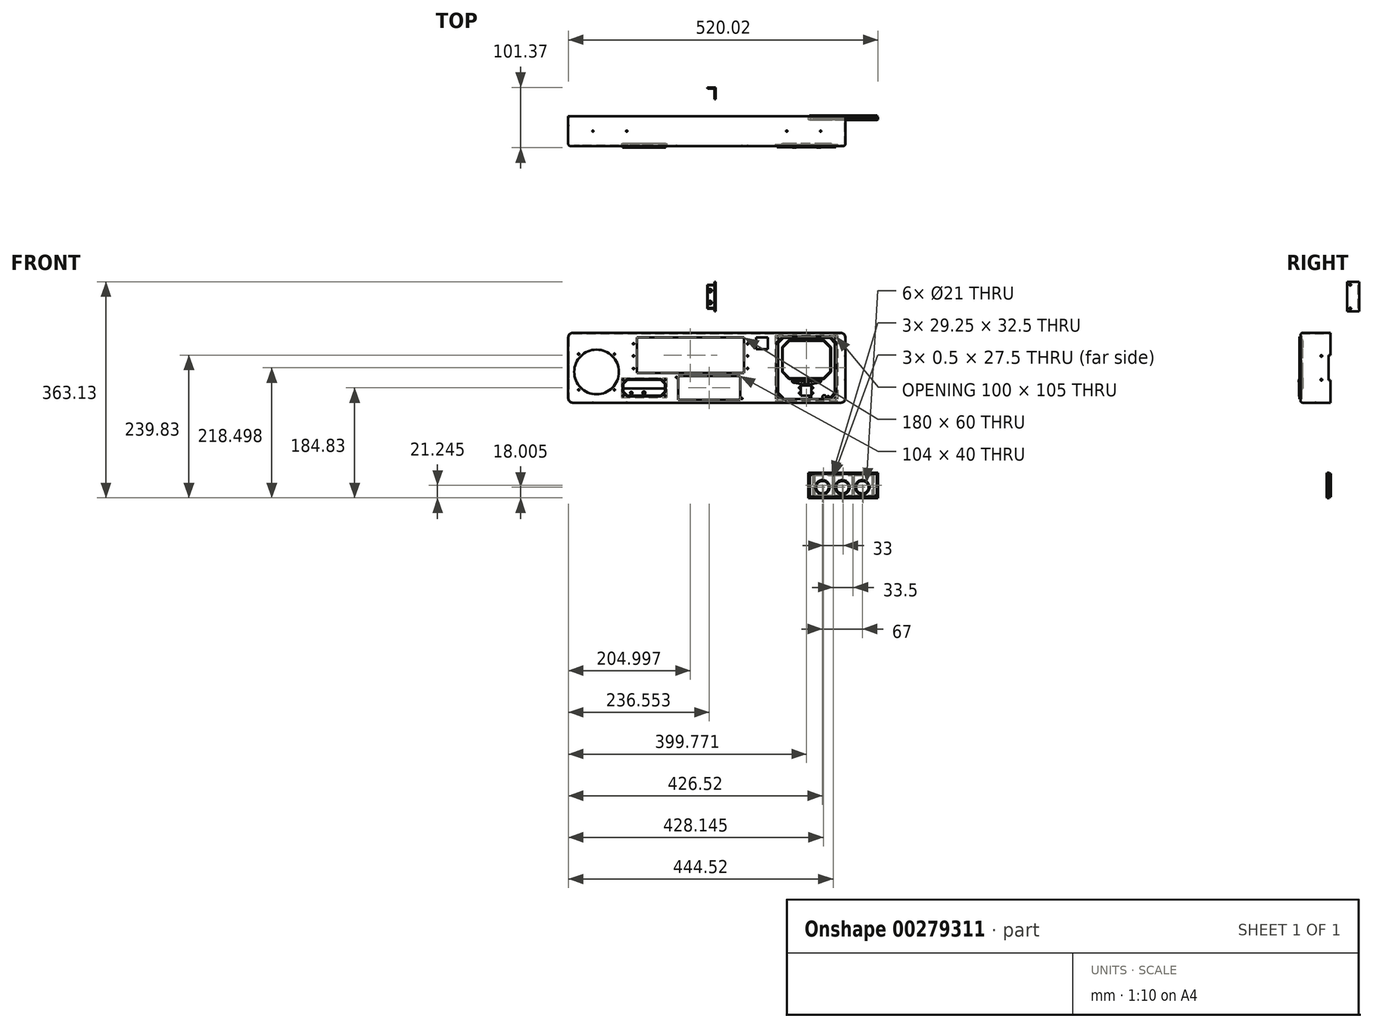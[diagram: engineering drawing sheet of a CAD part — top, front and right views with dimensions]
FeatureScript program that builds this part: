
annotation { "Feature Type Name" : "Feature", "Feature Type Description" : "" }
export const myFeature = defineFeature(function(context is Context, id is Id, definition is map)
    precondition{}
    {
        {
            var Q0;
            Q0=qCreatedBy(makeId("Front.planeOp"),FACE);
            var sketch = newSketch(context, id + "F0", { "sketchPlane" : qUnion([Q0])});
            skLineSegment(sketch, "E0.bottom", {"start": v(-245.15, 85.69) * mm, "end": v(219.85, 85.69) * mm});
            skLineSegment(sketch, "E0.top", {"start": v(-245.15, -31.31) * mm, "end": v(219.85, -31.31) * mm});
            skLineSegment(sketch, "E0.left", {"start": v(-245.15, 85.69) * mm, "end": v(-245.15, -31.31) * mm});
            skLineSegment(sketch, "E0.right", {"start": v(219.85, 85.69) * mm, "end": v(219.85, -31.31) * mm});
            skSolve(sketch);
        }
        {
            var Q0;
            Q0=qSketchRegion(id+"F0",true);
            var Q1;
            Q1=makeQuery(id+"F0.imprint","IMPRINT",FACE,{"disambiguationData":[TD([[makeQuery(id+"F0.imprint","IMPRINT",EDGE,{"derivedFrom":sQuery(id+"F0.wireOp",EDGE,"E0.bottom")}),-1.0]])]});
            extrude(context, id + "F1", {"entities" : qUnion([Q0, Q1]), "depth" : 50 * mm});
        }
        {
            var Q0;
            Q0=makeQuery(id+"F1.opExtrude","CAP_FACE",FACE,{"disambiguationData":[OSD([sQuery(id+"F0.wireOp",EDGE,"E0.bottom"),sQuery(id+"F0.wireOp",EDGE,"E0.top"),sQuery(id+"F0.wireOp",EDGE,"E0.left"),sQuery(id+"F0.wireOp",EDGE,"E0.right")])],"isStart":true});
            shell(context, id + "F2", {"entities" : qUnion([Q0]), "thickness" : 1 * mm});
        }
        {
            var Q0;
            Q0=makeQuery(id+"F1.opExtrude","CAP_FACE",FACE,{"disambiguationData":[OSD([sQuery(id+"F0.wireOp",EDGE,"E0.bottom"),sQuery(id+"F0.wireOp",EDGE,"E0.top"),sQuery(id+"F0.wireOp",EDGE,"E0.left"),sQuery(id+"F0.wireOp",EDGE,"E0.right")])],"isStart":false});
            var sketch = newSketch(context, id + "F3", { "sketchPlane" : qUnion([Q0])});
            skLineSegment(sketch, "E1.bottom", {"start": v(-130.15, 78.52) * mm, "end": v(49.85, 78.52) * mm});
            skLineSegment(sketch, "E1.top", {"start": v(-130.15, 18.52) * mm, "end": v(49.85, 18.52) * mm});
            skLineSegment(sketch, "E1.left", {"start": v(-130.15, 78.52) * mm, "end": v(-130.15, 18.52) * mm});
            skLineSegment(sketch, "E1.right", {"start": v(49.85, 78.52) * mm, "end": v(49.85, 18.52) * mm});
            skLineSegment(sketch, "E2.bottom", {"start": v(69.85, 78.32) * mm, "end": v(89.85, 78.32) * mm});
            skLineSegment(sketch, "E2.top", {"start": v(69.85, 58.32) * mm, "end": v(89.85, 58.32) * mm});
            skLineSegment(sketch, "E2.left", {"start": v(69.85, 78.32) * mm, "end": v(69.85, 58.32) * mm});
            skLineSegment(sketch, "E2.right", {"start": v(89.85, 78.32) * mm, "end": v(89.85, 58.32) * mm});
            skLineSegment(sketch, "E3.bottom", {"start": v(114.52, 79.69) * mm, "end": v(194.72, 79.69) * mm});
            skLineSegment(sketch, "E3.top", {"start": v(114.52, -25.31) * mm, "end": v(194.72, -25.31) * mm});
            skLineSegment(sketch, "E3.left", {"start": v(104.62, 69.79) * mm, "end": v(104.62, -15.41) * mm});
            skLineSegment(sketch, "E3.right", {"start": v(204.62, 69.79) * mm, "end": v(204.62, -15.41) * mm});
            skLineSegment(sketch, "E4.bottom", {"start": v(-128.05, -55.46) * mm, "end": v(-35.05, -55.46) * mm, "construction": true});
            skLineSegment(sketch, "E4.top", {"start": v(-128.05, -91.46) * mm, "end": v(-35.05, -91.46) * mm, "construction": true});
            skLineSegment(sketch, "E4.left", {"start": v(-128.05, -55.46) * mm, "end": v(-128.05, -91.46) * mm, "construction": true});
            skLineSegment(sketch, "E4.right", {"start": v(-35.05, -55.46) * mm, "end": v(-35.05, -91.46) * mm, "construction": true});
            skCircle(sketch, "E5", {"center": v(55.74, 67.55) * mm, "radius": 1.1 * mm});
            skCircle(sketch, "E6", {"center": v(55.74, 47.16) * mm, "radius": 1.1 * mm});
            skCircle(sketch, "E7", {"center": v(55.74, 26.05) * mm, "radius": 1.1 * mm});
            skLineSegment(sketch, "E8.bottom", {"start": v(-233.81, -59.67) * mm, "end": v(-156.81, -59.67) * mm, "construction": true});
            skLineSegment(sketch, "E8.top", {"start": v(-233.81, -136.67) * mm, "end": v(-156.81, -136.67) * mm, "construction": true});
            skLineSegment(sketch, "E8.left", {"start": v(-233.81, -59.67) * mm, "end": v(-233.81, -136.67) * mm, "construction": true});
            skLineSegment(sketch, "E8.right", {"start": v(-156.81, -59.67) * mm, "end": v(-156.81, -136.67) * mm, "construction": true});
            skCircle(sketch, "E9", {"center": v(106.12, 78.19) * mm, "radius": 1.1 * mm});
            skLineSegment(sketch, "E10", {"start": v(104.62, 69.79) * mm, "end": v(114.52, 79.69) * mm});
            skCircle(sketch, "E11", {"center": v(63.6, -74.48) * mm, "radius": 9.5 * mm});
            skLineSegment(sketch, "E12.bottom", {"start": v(46.65, -54.77) * mm, "end": v(139.65, -54.77) * mm});
            skLineSegment(sketch, "E12.top", {"start": v(46.65, -90.77) * mm, "end": v(139.65, -90.77) * mm});
            skLineSegment(sketch, "E12.left", {"start": v(46.65, -54.77) * mm, "end": v(46.65, -90.77) * mm});
            skLineSegment(sketch, "E12.right", {"start": v(139.65, -54.77) * mm, "end": v(139.65, -90.77) * mm});
            skCircle(sketch, "E13", {"center": v(93.62, -74.48) * mm, "radius": 9.5 * mm});
            skCircle(sketch, "E14", {"center": v(123.01, -74.48) * mm, "radius": 9.5 * mm});
            skCircle(sketch, "E15", {"center": v(50.65, -58.77) * mm, "radius": 1.5 * mm});
            skCircle(sketch, "E16", {"center": v(135.65, -86.77) * mm, "radius": 1.5 * mm});
            skLineSegment(sketch, "E17.bottom", {"start": v(-146.37, 8.19) * mm, "end": v(-89.37, 8.19) * mm});
            skLineSegment(sketch, "E17.top", {"start": v(-146.37, -20.81) * mm, "end": v(-89.37, -20.81) * mm});
            skLineSegment(sketch, "E17.left", {"start": v(-154.15, 0.4) * mm, "end": v(-154.15, -13.03) * mm});
            skLineSegment(sketch, "E17.right", {"start": v(-81.6, 0.4) * mm, "end": v(-81.6, -13.03) * mm});
            skLineSegment(sketch, "E18", {"start": v(104.62, -15.41) * mm, "end": v(114.52, -25.31) * mm});
            skLineSegment(sketch, "E19", {"start": v(194.72, -25.31) * mm, "end": v(204.62, -15.41) * mm});
            skLineSegment(sketch, "E20", {"start": v(194.72, 79.69) * mm, "end": v(204.62, 69.79) * mm});
            skCircle(sketch, "E21", {"center": v(105.72, -23.81) * mm, "radius": 1.1 * mm});
            skCircle(sketch, "E22", {"center": v(203.52, -23.81) * mm, "radius": 1.1 * mm});
            skCircle(sketch, "E23", {"center": v(203.12, 78.19) * mm, "radius": 1.1 * mm});
            skCircle(sketch, "E24", {"center": v(-197.65, 20.23) * mm, "radius": 37.5 * mm});
            skLineSegment(sketch, "E25", {"start": v(-154.15, 0.4) * mm, "end": v(-146.37, 8.19) * mm});
            skLineSegment(sketch, "E26", {"start": v(-89.37, 8.19) * mm, "end": v(-81.6, 0.4) * mm});
            skLineSegment(sketch, "E27", {"start": v(-81.6, -13.03) * mm, "end": v(-89.37, -20.81) * mm});
            skLineSegment(sketch, "E28", {"start": v(-154.15, -13.03) * mm, "end": v(-146.37, -20.81) * mm});
            skCircle(sketch, "E29", {"center": v(-135.7, 67.55) * mm, "radius": 1.1 * mm});
            skCircle(sketch, "E30", {"center": v(-135.7, 47.16) * mm, "radius": 1.1 * mm});
            skCircle(sketch, "E31", {"center": v(-135.7, 26.05) * mm, "radius": 1.1 * mm});
            skCircle(sketch, "E32", {"center": v(-227.65, 50.23) * mm, "radius": 1.1 * mm});
            skCircle(sketch, "E33", {"center": v(-227.65, -9.77) * mm, "radius": 1.1 * mm});
            skCircle(sketch, "E34", {"center": v(-167.65, -9.77) * mm, "radius": 1.1 * mm});
            skCircle(sketch, "E35", {"center": v(-167.65, 50.23) * mm, "radius": 1.1 * mm});
            skCircle(sketch, "E36", {"center": v(-63.6, 11.29) * mm, "radius": 1.1 * mm});
            skCircle(sketch, "E37", {"center": v(46.4, -24.21) * mm, "radius": 1.1 * mm});
            skLineSegment(sketch, "E38.bottom", {"start": v(-60.6, 13.52) * mm, "end": v(43.4, 13.52) * mm});
            skLineSegment(sketch, "E38.top", {"start": v(-60.6, -26.48) * mm, "end": v(43.4, -26.48) * mm});
            skLineSegment(sketch, "E38.left", {"start": v(-60.6, 13.52) * mm, "end": v(-60.6, -26.48) * mm});
            skLineSegment(sketch, "E38.right", {"start": v(43.4, 13.52) * mm, "end": v(43.4, -26.48) * mm});
            skLineSegment(sketch, "E39", {"start": v(-230.37, -45.58) * mm, "end": v(-80.37, -45.58) * mm, "construction": true});
            skLineSegment(sketch, "E40", {"start": v(-255.4, -26.53) * mm, "end": v(-255.4, 68.47) * mm, "construction": true});
            skLineSegment(sketch, "E41", {"start": v(-239.28, 22.84) * mm, "end": v(-239.28, -34.99) * mm, "construction": true});
            skLineSegment(sketch, "E42.bottom", {"start": v(-167.65, -9.77) * mm, "end": v(-227.65, -9.77) * mm, "construction": true});
            skLineSegment(sketch, "E42.top", {"start": v(-167.65, 50.23) * mm, "end": v(-227.65, 50.23) * mm, "construction": true});
            skLineSegment(sketch, "E42.left", {"start": v(-167.65, -9.77) * mm, "end": v(-167.65, 50.23) * mm, "construction": true});
            skLineSegment(sketch, "E42.right", {"start": v(-227.65, -9.77) * mm, "end": v(-227.65, 50.23) * mm, "construction": true});
            skSolve(sketch);
        }
        {
            var Q0;
            Q0=makeQuery(id+"F1.opExtrude","SWEPT_EDGE",EDGE,{"disambiguationData":[OSD([sQuery(id+"F0.wireOp",EDGE,"E0.bottom"),sQuery(id+"F0.wireOp",EDGE,"E0.left")])]});
            var Q1;
            Q1=makeQuery(id+"F1.opExtrude","SWEPT_EDGE",EDGE,{"disambiguationData":[OSD([sQuery(id+"F0.wireOp",EDGE,"E0.bottom"),sQuery(id+"F0.wireOp",EDGE,"E0.right")])]});
            var Q2;
            Q2=makeQuery(id+"F1.opExtrude","SWEPT_EDGE",EDGE,{"disambiguationData":[OSD([sQuery(id+"F0.wireOp",EDGE,"E0.top"),sQuery(id+"F0.wireOp",EDGE,"E0.right")])]});
            var Q3;
            Q3=makeQuery(id+"F1.opExtrude","SWEPT_EDGE",EDGE,{"disambiguationData":[OSD([sQuery(id+"F0.wireOp",EDGE,"E0.top"),sQuery(id+"F0.wireOp",EDGE,"E0.left")])]});
            var Q4;
            Q4=makeQuery(id+"F2.opShell","OFFSET_EDGE",EDGE,{"disambiguationData":[OSD([sQuery(id+"F0.wireOp",EDGE,"E0.bottom"),sQuery(id+"F0.wireOp",EDGE,"E0.left")])]});
            var Q5;
            Q5=makeQuery(id+"F2.opShell","OFFSET_EDGE",EDGE,{"disambiguationData":[OSD([sQuery(id+"F0.wireOp",EDGE,"E0.top"),sQuery(id+"F0.wireOp",EDGE,"E0.left")])]});
            var Q6;
            Q6=makeQuery(id+"F2.opShell","OFFSET_EDGE",EDGE,{"disambiguationData":[OSD([sQuery(id+"F0.wireOp",EDGE,"E0.top"),sQuery(id+"F0.wireOp",EDGE,"E0.right")])]});
            var Q7;
            Q7=makeQuery(id+"F2.opShell","OFFSET_EDGE",EDGE,{"disambiguationData":[OSD([sQuery(id+"F0.wireOp",EDGE,"E0.bottom"),sQuery(id+"F0.wireOp",EDGE,"E0.right")])]});
            fillet(context, id + "F4", {"entities" : qUnion([Q0, Q1, Q2, Q3, Q4, Q5, Q6, Q7]), "radius" : 7 * mm, "tangentPropagation" : true, "allowEdgeOverflow" : false});
        }
        {
            var Q0;
            Q0=qSketchRegion(id+"F3",true);
            extrude(context, id + "F5", {"entities" : qUnion([Q0]), "operationType" : NewBodyOperationType.REMOVE, "oppositeDirection" : true, "depth" : 25 * mm});
        }
        {
            var Q0;
            {var subQ0=sQuery(id+"F0.wireOp",EDGE,"E0.right");var subQ1=sQuery(id+"F0.wireOp",EDGE,"E0.bottom");Q0=makeQuery(id+"F4.opFillet","BLEND_EDGE",EDGE,{"blendedFrom":[makeQuery(id+"F1.opExtrude","SWEPT_EDGE",EDGE,{"disambiguationData":[OSD([subQ1,subQ0])]}),makeQuery(id+"F1.opExtrude","CAP_FACE",FACE,{"disambiguationData":[OSD([subQ1,sQuery(id+"F0.wireOp",EDGE,"E0.top"),sQuery(id+"F0.wireOp",EDGE,"E0.left"),subQ0])],"isStart":false})],"blendedInto":[makeQuery(id+"F1.opExtrude","CAP_FACE",FACE,{"disambiguationData":[OSD([subQ1,sQuery(id+"F0.wireOp",EDGE,"E0.top"),sQuery(id+"F0.wireOp",EDGE,"E0.left"),subQ0])],"isStart":false})]});}
            fillet(context, id + "F6", {"entities" : qUnion([Q0]), "radius" : 3 * mm, "tangentPropagation" : true, "allowEdgeOverflow" : false});
        }
        {
            var Q0;
            Q0=makeQuery(id+"F1.opExtrude","SWEPT_FACE",FACE,{"disambiguationData":[OSD([sQuery(id+"F0.wireOp",EDGE,"E0.left")])]});
            var sketch = newSketch(context, id + "F7", { "sketchPlane" : qUnion([Q0])});
            skCircle(sketch, "E43", {"center": v(15, 47.19) * mm, "radius": 1.5 * mm});
            skCircle(sketch, "E44", {"center": v(15, 7.19) * mm, "radius": 1.5 * mm});
            skLineSegment(sketch, "E45", {"start": v(-16.01, 27.19) * mm, "end": v(37.35, 27.19) * mm, "construction": true});
            skPoint(sketch, "E46.middle.positionSnap0", {"position": v(0, 27.19) * mm});
            skPoint(sketch, "E46.centerSnap0", {"position": v(0, 27.19) * mm});
            skLineSegment(sketch, "E47.bottom", {"start": v(3, 6.19) * mm, "end": v(0, 6.19) * mm});
            skLineSegment(sketch, "E47.top", {"start": v(3, 48.19) * mm, "end": v(0, 48.19) * mm});
            skLineSegment(sketch, "E47.left", {"start": v(3, 6.19) * mm, "end": v(3, 48.19) * mm});
            skLineSegment(sketch, "E47.right", {"start": v(0, 6.19) * mm, "end": v(0, 48.19) * mm});
            skPoint(sketch, "E47.middle", {"position": v(1.5, 27.19) * mm});
            skSolve(sketch);
        }
        {
            var Q0;
            Q0=qSketchRegion(id+"F7",true);
            extrude(context, id + "F8", {"entities" : qUnion([Q0]), "operationType" : NewBodyOperationType.REMOVE, "oppositeDirection" : true, "depth" : 500 * mm});
        }
        {
            var Q0;
            Q0=qCreatedBy(makeId("Right.planeOp"),FACE);
            var sketch = newSketch(context, id + "F9", { "sketchPlane" : qUnion([Q0])});
            skLineSegment(sketch, "E48.bottom", {"start": v(28.37, 121.82) * mm, "end": v(48.37, 121.82) * mm});
            skLineSegment(sketch, "E48.top", {"start": v(28.37, 171.82) * mm, "end": v(48.37, 171.82) * mm});
            skLineSegment(sketch, "E48.left", {"start": v(28.37, 121.82) * mm, "end": v(28.37, 171.82) * mm});
            skLineSegment(sketch, "E48.right", {"start": v(48.37, 121.82) * mm, "end": v(48.37, 171.82) * mm});
            skPoint(sketch, "E48.middle", {"position": v(38.37, 146.82) * mm});
            skCircle(sketch, "E49", {"center": v(33.37, 166.82) * mm, "radius": 1.5 * mm});
            skCircle(sketch, "E50", {"center": v(33.37, 126.82) * mm, "radius": 1.5 * mm});
            skSolve(sketch);
        }
        {
            var Q0;
            Q0=qSketchRegion(id+"F9",true);
            extrude(context, id + "F10", {"entities" : qUnion([Q0]), "depth" : 2 * mm});
        }
        {
            var Q0;
            Q0=makeQuery(id+"F10.opExtrude","SWEPT_FACE",FACE,{"disambiguationData":[OSD([sQuery(id+"F9.wireOp",EDGE,"E48.right")])]});
            var sketch = newSketch(context, id + "F11", { "sketchPlane" : qUnion([Q0])});
            skLineSegment(sketch, "E51.bottom", {"start": v(0, 166.82) * mm, "end": v(12, 166.82) * mm});
            skLineSegment(sketch, "E51.top", {"start": v(0, 126.82) * mm, "end": v(12, 126.82) * mm});
            skLineSegment(sketch, "E51.left", {"start": v(0, 166.82) * mm, "end": v(0, 126.82) * mm});
            skLineSegment(sketch, "E51.right", {"start": v(12, 166.82) * mm, "end": v(12, 126.82) * mm});
            skSolve(sketch);
        }
        {
            var Q0;
            Q0=qSketchRegion(id+"F11",true);
            extrude(context, id + "F12", {"entities" : qUnion([Q0]), "operationType" : NewBodyOperationType.ADD, "oppositeDirection" : true, "depth" : 2 * mm});
        }
        {
            var Q0;
            Q0=makeQuery(id+"F12.opExtrude","CAP_FACE",FACE,{"disambiguationData":[OSD([sQuery(id+"F11.wireOp",EDGE,"E51.bottom"),sQuery(id+"F11.wireOp",EDGE,"E51.top"),sQuery(id+"F11.wireOp",EDGE,"E51.left"),sQuery(id+"F11.wireOp",EDGE,"E51.right")])],"isStart":false});
            var sketch = newSketch(context, id + "F13", { "sketchPlane" : qUnion([Q0])});
            skCircle(sketch, "E52", {"center": v(-7, 156.82) * mm, "radius": 1.5 * mm});
            skCircle(sketch, "E53", {"center": v(-7, 136.82) * mm, "radius": 1.5 * mm});
            skSolve(sketch);
        }
        {
            var Q0;
            Q0=sQuery(id+"F13.wireOp",VERTEX,"E52.center");
            var Q1;
            Q1=sQuery(id+"F13.wireOp",VERTEX,"E53.center");
            var Q2;
            Q2=makeQuery(id+"F10.opExtrude","SWEPT_BODY",BODY,{"disambiguationData":[OSD([sQuery(id+"F9.wireOp",EDGE,"E48.bottom"),sQuery(id+"F9.wireOp",EDGE,"E48.top"),sQuery(id+"F9.wireOp",EDGE,"E48.left"),sQuery(id+"F9.wireOp",EDGE,"E48.right"),sQuery(id+"F9.wireOp",EDGE,"E49"),sQuery(id+"F9.wireOp",EDGE,"E50")])]});
            hole(context, id + "F14", {"style" : HoleStyle.C_SINK, "endStyle" : HoleEndStyle.THROUGH, "holeDiameter" : 3 * mm, "cSinkDiameter" : 5.7 * mm, "cSinkAngle" : 90 * degree, "locations" : qUnion([Q0, Q1]), "scope" : qUnion([Q2]), "isTappedThrough" : true});
        }
        {
            var Q0;
            Q0=makeQuery(id+"F12.opExtrude","CAP_EDGE",EDGE,{"disambiguationData":[OSD([sQuery(id+"F11.wireOp",EDGE,"E51.bottom")])],"isStart":false});
            var Q1;
            Q1=makeQuery(id+"F12.opExtrude","CAP_EDGE",EDGE,{"disambiguationData":[OSD([sQuery(id+"F11.wireOp",EDGE,"E51.right")])],"isStart":false});
            var Q2;
            Q2=makeQuery(id+"F12.opExtrude","CAP_EDGE",EDGE,{"disambiguationData":[OSD([sQuery(id+"F11.wireOp",EDGE,"E51.top")])],"isStart":false});
            chamfer(context, id + "F15", {"entities" : qUnion([Q0, Q1, Q2]), "width" : 1 * mm, "tangentPropagation" : true});
        }
        {
            var Q0;
            Q0=qCreatedBy(makeId("Front.planeOp"),FACE);
            var sketch = newSketch(context, id + "F16", { "sketchPlane" : qUnion([Q0])});
            skLineSegment(sketch, "E54.bottom", {"start": v(164.87, -150.31) * mm, "end": v(267.87, -150.31) * mm});
            skLineSegment(sketch, "E54.top", {"start": v(164.87, -189.81) * mm, "end": v(267.87, -189.81) * mm});
            skLineSegment(sketch, "E54.left", {"start": v(164.87, -150.31) * mm, "end": v(164.87, -189.81) * mm});
            skLineSegment(sketch, "E54.right", {"start": v(267.87, -150.31) * mm, "end": v(267.87, -189.81) * mm});
            skLineSegment(sketch, "E55.bottom", {"start": v(164.87, -150.31) * mm, "end": v(159.37, -150.31) * mm});
            skLineSegment(sketch, "E55.top", {"start": v(164.87, -154.31) * mm, "end": v(159.37, -154.31) * mm});
            skLineSegment(sketch, "E55.left", {"start": v(164.87, -150.31) * mm, "end": v(164.87, -154.31) * mm});
            skLineSegment(sketch, "E55.right", {"start": v(159.37, -150.31) * mm, "end": v(159.37, -154.31) * mm});
            skLineSegment(sketch, "E56.bottom", {"start": v(267.87, -189.81) * mm, "end": v(273.37, -189.81) * mm});
            skLineSegment(sketch, "E56.top", {"start": v(267.87, -185.81) * mm, "end": v(273.37, -185.81) * mm});
            skLineSegment(sketch, "E56.left", {"start": v(267.87, -189.81) * mm, "end": v(267.87, -185.81) * mm});
            skLineSegment(sketch, "E56.right", {"start": v(273.37, -189.81) * mm, "end": v(273.37, -185.81) * mm});
            skCircle(sketch, "E57", {"center": v(161.37, -152.31) * mm, "radius": 1.1 * mm});
            skCircle(sketch, "E58", {"center": v(271.37, -187.81) * mm, "radius": 1.1 * mm});
            skSolve(sketch);
        }
        {
            var Q0;
            Q0=makeQuery(id+"F16.imprint","IMPRINT",FACE,{"disambiguationData":[TD([[makeQuery(id+"F16.imprint","IMPRINT",EDGE,{"derivedFrom":sQuery(id+"F16.wireOp",EDGE,"E54.bottom")}),-1.0]])]});
            extrude(context, id + "F17", {"entities" : qUnion([Q0]), "depth" : 1 * mm, "hasSecondDirection" : true, "secondDirectionOppositeDirection" : true, "secondDirectionDepth" : 1 * mm});
        }
        {
            var Q0;
            Q0=makeQuery(id+"F16.imprint","IMPRINT",FACE,{"disambiguationData":[TD([[makeQuery(id+"F16.imprint","IMPRINT",EDGE,{"derivedFrom":sQuery(id+"F16.wireOp",EDGE,"E55.bottom")}),1.0]])]});
            var Q1;
            Q1=makeQuery(id+"F16.imprint","IMPRINT",FACE,{"disambiguationData":[TD([[makeQuery(id+"F16.imprint","IMPRINT",EDGE,{"derivedFrom":sQuery(id+"F16.wireOp",EDGE,"E56.bottom")}),1.0]])]});
            extrude(context, id + "F18", {"entities" : qUnion([Q0, Q1]), "operationType" : NewBodyOperationType.ADD, "depth" : 1 * mm, "hasSecondDirection" : true, "secondDirectionOppositeDirection" : true, "secondDirectionDepth" : 1 * mm});
        }
        {
            var Q0;
            Q0=makeQuery(id+"F17.opExtrude","CAP_FACE",FACE,{"disambiguationData":[OSD([sQuery(id+"F16.wireOp",EDGE,"E54.bottom"),sQuery(id+"F16.wireOp",EDGE,"E54.top"),sQuery(id+"F16.wireOp",EDGE,"E54.left"),sQuery(id+"F16.wireOp",EDGE,"E54.right"),sQuery(id+"F16.wireOp",EDGE,"E55.left"),sQuery(id+"F16.wireOp",EDGE,"E56.left")])],"isStart":false});
            var sketch = newSketch(context, id + "F19", { "sketchPlane" : qUnion([Q0])});
            skLineSegment(sketch, "E59.bottom", {"start": v(164.87, -150.31) * mm, "end": v(267.87, -150.31) * mm});
            skLineSegment(sketch, "E59.top", {"start": v(164.87, -189.81) * mm, "end": v(267.87, -189.81) * mm});
            skLineSegment(sketch, "E59.left", {"start": v(164.87, -150.31) * mm, "end": v(164.87, -189.81) * mm});
            skLineSegment(sketch, "E59.right", {"start": v(267.87, -150.31) * mm, "end": v(267.87, -189.81) * mm});
            skLineSegment(sketch, "E60.bottom", {"start": v(165.87, -151.31) * mm, "end": v(266.87, -151.31) * mm});
            skLineSegment(sketch, "E60.top", {"start": v(165.87, -188.81) * mm, "end": v(266.87, -188.81) * mm});
            skLineSegment(sketch, "E60.left", {"start": v(165.87, -151.31) * mm, "end": v(165.87, -188.81) * mm});
            skLineSegment(sketch, "E60.right", {"start": v(266.87, -151.31) * mm, "end": v(266.87, -188.81) * mm});
            skSolve(sketch);
        }
        {
            var Q0;
            Q0=qSketchRegion(id+"F19",true);
            extrude(context, id + "F20", {"entities" : qUnion([Q0]), "operationType" : NewBodyOperationType.ADD, "depth" : 2.5 * mm});
        }
        {
            var Q0;
            Q0=makeQuery(id+"F19.imprint","IMPRINT",FACE,{"disambiguationData":[TD([[makeQuery(id+"F19.imprint","IMPRINT",EDGE,{"derivedFrom":sQuery(id+"F19.wireOp",EDGE,"E60.bottom")}),-1.0]])]});
            var sketch = newSketch(context, id + "F21", { "sketchPlane" : qUnion([Q0])});
            skLineSegment(sketch, "E61.bottom", {"start": v(199.12, -156.31) * mm, "end": v(199.62, -156.31) * mm});
            skLineSegment(sketch, "E61.top", {"start": v(199.12, -183.81) * mm, "end": v(199.62, -183.81) * mm});
            skLineSegment(sketch, "E61.left", {"start": v(199.12, -156.31) * mm, "end": v(199.12, -183.81) * mm});
            skLineSegment(sketch, "E61.right", {"start": v(199.62, -156.31) * mm, "end": v(199.62, -183.81) * mm});
            skLineSegment(sketch, "E62.bottom", {"start": v(232.62, -156.31) * mm, "end": v(233.12, -156.31) * mm});
            skLineSegment(sketch, "E62.top", {"start": v(232.62, -183.81) * mm, "end": v(233.12, -183.81) * mm});
            skLineSegment(sketch, "E62.left", {"start": v(232.62, -156.31) * mm, "end": v(232.62, -183.81) * mm});
            skLineSegment(sketch, "E62.right", {"start": v(233.12, -156.31) * mm, "end": v(233.12, -183.81) * mm});
            skLineSegment(sketch, "E63.bottom", {"start": v(266.12, -156.31) * mm, "end": v(266.62, -156.31) * mm});
            skLineSegment(sketch, "E63.top", {"start": v(266.12, -183.81) * mm, "end": v(266.62, -183.81) * mm});
            skLineSegment(sketch, "E63.left", {"start": v(266.12, -156.31) * mm, "end": v(266.12, -183.81) * mm});
            skLineSegment(sketch, "E63.right", {"start": v(266.62, -156.31) * mm, "end": v(266.62, -183.81) * mm});
            skSolve(sketch);
        }
        {
            var Q0;
            Q0=qSketchRegion(id+"F21",true);
            extrude(context, id + "F22", {"entities" : qUnion([Q0]), "operationType" : NewBodyOperationType.REMOVE, "oppositeDirection" : true, "depth" : 3 * mm});
        }
        {
            var Q0;
            Q0=makeQuery(id+"F2.opShell","OFFSET_FACE",FACE,{"disambiguationData":[OSD([sQuery(id+"F0.wireOp",EDGE,"E0.bottom"),sQuery(id+"F0.wireOp",EDGE,"E0.top"),sQuery(id+"F0.wireOp",EDGE,"E0.left"),sQuery(id+"F0.wireOp",EDGE,"E0.right")])]});
            var sketch = newSketch(context, id + "F23", { "sketchPlane" : qUnion([Q0])});
            skLineSegment(sketch, "E64.bottom", {"start": v(156.15, 10.19) * mm, "end": v(79.6, 10.19) * mm});
            skLineSegment(sketch, "E64.top", {"start": v(156.15, -22.81) * mm, "end": v(79.6, -22.81) * mm});
            skLineSegment(sketch, "E64.left", {"start": v(156.15, 10.19) * mm, "end": v(156.15, -22.81) * mm});
            skLineSegment(sketch, "E64.right", {"start": v(79.6, 10.19) * mm, "end": v(79.6, -22.81) * mm});
            skSolve(sketch);
        }
        {
            var Q0;
            Q0=qSketchRegion(id+"F23",true);
            extrude(context, id + "F24", {"entities" : qUnion([Q0]), "depth" : 1 * mm});
        }
        {
            var Q0;
            Q0=makeQuery(id+"F3.imprint","IMPRINT",FACE,{"disambiguationData":[TD([[makeQuery(id+"F3.imprint","IMPRINT",EDGE,{"derivedFrom":sQuery(id+"F3.wireOp",EDGE,"E1.bottom")}),1.0]])]});
            var sketch = newSketch(context, id + "F25", { "sketchPlane" : qUnion([Q0])});
            skCircle(sketch, "E65", {"center": v(-153.05, 7.09) * mm, "radius": 1.1 * mm});
            skCircle(sketch, "E66", {"center": v(-153.05, -19.71) * mm, "radius": 1.1 * mm});
            skCircle(sketch, "E67", {"center": v(-82.7, 7.09) * mm, "radius": 1.1 * mm});
            skCircle(sketch, "E68", {"center": v(-82.7, -19.71) * mm, "radius": 1.1 * mm});
            skSolve(sketch);
        }
        {
            var Q0;
            Q0=qSketchRegion(id+"F25",true);
            extrude(context, id + "F26", {"entities" : qUnion([Q0]), "operationType" : NewBodyOperationType.REMOVE, "oppositeDirection" : true, "depth" : 5 * mm});
        }
        {
            var Q0;
            Q0=makeQuery(id+"F3.imprint","IMPRINT",FACE,{"disambiguationData":[TD([[makeQuery(id+"F3.imprint","IMPRINT",EDGE,{"derivedFrom":sQuery(id+"F3.wireOp",EDGE,"E17.bottom")}),-1.0]])]});
            var sketch = newSketch(context, id + "F27", { "sketchPlane" : qUnion([Q0])});
            skLineSegment(sketch, "E69.bottom", {"start": v(-146.33, 8.09) * mm, "end": v(-89.47, 8.09) * mm});
            skLineSegment(sketch, "E69.top", {"start": v(-146.33, -20.71) * mm, "end": v(-89.42, -20.71) * mm});
            skLineSegment(sketch, "E69.left", {"start": v(-154.05, 0.37) * mm, "end": v(-154.05, -13) * mm});
            skLineSegment(sketch, "E69.right", {"start": v(-81.7, 0.3) * mm, "end": v(-81.7, -13) * mm});
            skLineSegment(sketch, "E70", {"start": v(-154.05, 0.37) * mm, "end": v(-146.33, 8.09) * mm});
            skLineSegment(sketch, "E71", {"start": v(-89.47, 8.09) * mm, "end": v(-81.7, 0.3) * mm});
            skLineSegment(sketch, "E72", {"start": v(-81.7, -13) * mm, "end": v(-89.42, -20.71) * mm});
            skLineSegment(sketch, "E73", {"start": v(-154.05, -13) * mm, "end": v(-146.33, -20.71) * mm});
            skLineSegment(sketch, "E74", {"start": v(-146.14, 7.09) * mm, "end": v(-89.89, 7.09) * mm});
            skLineSegment(sketch, "E75", {"start": v(-89.89, 7.09) * mm, "end": v(-82.7, -0.1) * mm});
            skLineSegment(sketch, "E76", {"start": v(-82.7, -0.1) * mm, "end": v(-82.7, -12.58) * mm});
            skLineSegment(sketch, "E77", {"start": v(-82.7, -12.58) * mm, "end": v(-89.83, -19.71) * mm});
            skLineSegment(sketch, "E78", {"start": v(-89.83, -19.71) * mm, "end": v(-145.93, -19.71) * mm});
            skLineSegment(sketch, "E79", {"start": v(-145.93, -19.71) * mm, "end": v(-153.05, -12.58) * mm});
            skLineSegment(sketch, "E80", {"start": v(-153.05, -12.58) * mm, "end": v(-153.05, -0.17) * mm});
            skLineSegment(sketch, "E81", {"start": v(-153.05, -0.17) * mm, "end": v(-146.14, 7.09) * mm});
            skSolve(sketch);
        }
        {
            var Q0;
            Q0=qSketchRegion(id+"F27",true);
            extrude(context, id + "F28", {"entities" : qUnion([Q0]), "operationType" : NewBodyOperationType.ADD, "depth" : 1 * mm, "hasSecondDirection" : true, "secondDirectionOppositeDirection" : true, "secondDirectionDepth" : 2 * mm});
        }
        {
            var Q0;
            Q0=makeQuery(id+"F27.imprint","IMPRINT",FACE,{"disambiguationData":[TD([[makeQuery(id+"F27.imprint","IMPRINT",EDGE,{"derivedFrom":sQuery(id+"F27.wireOp",EDGE,"E74")}),-1.0]])]});
            var sketch = newSketch(context, id + "F29", { "sketchPlane" : qUnion([Q0])});
            skLineSegment(sketch, "E82", {"start": v(-145.81, 7.09) * mm, "end": v(-89.89, 7.09) * mm});
            skLineSegment(sketch, "E83", {"start": v(-89.89, 7.09) * mm, "end": v(-82.7, -0.1) * mm});
            skLineSegment(sketch, "E84", {"start": v(-82.7, -0.1) * mm, "end": v(-82.7, -7.17) * mm});
            skLineSegment(sketch, "E85", {"start": v(-153.05, -7.17) * mm, "end": v(-153.05, -0.17) * mm});
            skLineSegment(sketch, "E86", {"start": v(-153.05, -0.17) * mm, "end": v(-145.81, 7.09) * mm});
            skLineSegment(sketch, "E87", {"start": v(-153.05, -7.17) * mm, "end": v(-82.7, -7.17) * mm});
            skSolve(sketch);
        }
        {
            var Q0;
            Q0=qSketchRegion(id+"F29",true);
            extrude(context, id + "F30", {"entities" : qUnion([Q0]), "operationType" : NewBodyOperationType.REMOVE, "oppositeDirection" : true, "depth" : 3 * mm});
        }
        {
            var Q0;
            Q0=makeQuery(id+"F28.opExtrude","CAP_FACE",FACE,{"disambiguationData":[OSD([sQuery(id+"F27.wireOp",EDGE,"E69.bottom"),sQuery(id+"F27.wireOp",EDGE,"E69.top"),sQuery(id+"F27.wireOp",EDGE,"E69.left"),sQuery(id+"F27.wireOp",EDGE,"E69.right"),sQuery(id+"F27.wireOp",EDGE,"E70"),sQuery(id+"F27.wireOp",EDGE,"E71"),sQuery(id+"F27.wireOp",EDGE,"E72"),sQuery(id+"F27.wireOp",EDGE,"E73"),sQuery(id+"F27.wireOp",EDGE,"E74"),sQuery(id+"F27.wireOp",EDGE,"E75"),sQuery(id+"F27.wireOp",EDGE,"E76"),sQuery(id+"F27.wireOp",EDGE,"E77"),sQuery(id+"F27.wireOp",EDGE,"E78"),sQuery(id+"F27.wireOp",EDGE,"E79"),sQuery(id+"F27.wireOp",EDGE,"E80"),sQuery(id+"F27.wireOp",EDGE,"E81")])],"isStart":false});
            extrude(context, id + "F31", {"entities" : qUnion([Q0]), "depth" : 1.5 * mm});
        }
        {
            var Q0;
            Q0=makeQuery(id+"F28.boolean.opBoolean","SPLIT",FACE,{"disambiguationData":[TD([makeQuery(id+"F28.opExtrude","SWEPT_FACE",FACE,{"disambiguationData":[OSD([sQuery(id+"F27.wireOp",EDGE,"E74")])]})])],"derivedFrom":makeQuery(id+"F24.opExtrude","CAP_FACE",FACE,{"disambiguationData":[OSD([sQuery(id+"F23.wireOp",EDGE,"E64.bottom"),sQuery(id+"F23.wireOp",EDGE,"E64.top"),sQuery(id+"F23.wireOp",EDGE,"E64.left"),sQuery(id+"F23.wireOp",EDGE,"E64.right")])],"isStart":true})});
            var sketch = newSketch(context, id + "F32", { "sketchPlane" : qUnion([Q0])});
            skCircle(sketch, "E88", {"center": v(-139.31, -14.97) * mm, "radius": 2 * mm});
            skSolve(sketch);
        }
        {
            var Q0;
            Q0=makeQuery(id+"F32.imprint","IMPRINT",FACE,{"disambiguationData":[TD([[makeQuery(id+"F32.imprint","IMPRINT",EDGE,{"derivedFrom":sQuery(id+"F32.wireOp",EDGE,"E88")}),-1.0]])]});
            var sketch = newSketch(context, id + "F33", { "sketchPlane" : qUnion([Q0])});
            skCircle(sketch, "E89", {"center": v(-118.17, -14.77) * mm, "radius": 2.5 * mm});
            skSolve(sketch);
        }
        {
            var Q0;
            Q0=qSketchRegion(id+"F32",true);
            extrude(context, id + "F34", {"entities" : qUnion([Q0]), "operationType" : NewBodyOperationType.REMOVE, "oppositeDirection" : true, "depth" : 2 * mm});
        }
        {
            var Q0;
            Q0=qSketchRegion(id+"F33",true);
            extrude(context, id + "F35", {"entities" : qUnion([Q0]), "operationType" : NewBodyOperationType.REMOVE, "oppositeDirection" : true, "depth" : 2 * mm});
        }
        {
            var Q0;
            Q0=makeQuery(id+"F20.opExtrude","CAP_FACE",FACE,{"disambiguationData":[OSD([sQuery(id+"F19.wireOp",EDGE,"E59.bottom"),sQuery(id+"F19.wireOp",EDGE,"E59.top"),sQuery(id+"F19.wireOp",EDGE,"E59.left"),sQuery(id+"F19.wireOp",EDGE,"E59.right"),sQuery(id+"F19.wireOp",EDGE,"E60.bottom"),sQuery(id+"F19.wireOp",EDGE,"E60.top"),sQuery(id+"F19.wireOp",EDGE,"E60.left"),sQuery(id+"F19.wireOp",EDGE,"E60.right")])],"isStart":false});
            var sketch = newSketch(context, id + "F36", { "sketchPlane" : qUnion([Q0])});
            skLineSegment(sketch, "E90.bottom", {"start": v(157.87, -148.81) * mm, "end": v(274.87, -148.81) * mm});
            skLineSegment(sketch, "E90.top", {"start": v(157.87, -191.31) * mm, "end": v(274.87, -191.31) * mm});
            skLineSegment(sketch, "E90.left", {"start": v(157.87, -148.81) * mm, "end": v(157.87, -191.31) * mm});
            skLineSegment(sketch, "E90.right", {"start": v(274.87, -148.81) * mm, "end": v(274.87, -191.31) * mm});
            skSolve(sketch);
        }
        {
            var Q0;
            Q0=qSketchRegion(id+"F36",true);
            extrude(context, id + "F37", {"entities" : qUnion([Q0]), "depth" : 2 * mm});
        }
        {
            var Q0;
            Q0=makeQuery(id+"F24.opExtrude","CAP_FACE",FACE,{"disambiguationData":[OSD([sQuery(id+"F23.wireOp",EDGE,"E64.bottom"),sQuery(id+"F23.wireOp",EDGE,"E64.top"),sQuery(id+"F23.wireOp",EDGE,"E64.left"),sQuery(id+"F23.wireOp",EDGE,"E64.right")])],"isStart":false});
            var sketch = newSketch(context, id + "F38", { "sketchPlane" : qUnion([Q0])});
            skLineSegment(sketch, "E91", {"start": v(153.05, -0.17) * mm, "end": v(145.81, 7.09) * mm});
            skLineSegment(sketch, "E92", {"start": v(145.81, 7.09) * mm, "end": v(89.89, 7.09) * mm});
            skLineSegment(sketch, "E93", {"start": v(89.89, 7.09) * mm, "end": v(82.7, -0.1) * mm});
            skLineSegment(sketch, "E94", {"start": v(82.7, -0.1) * mm, "end": v(82.7, -7.17) * mm});
            skLineSegment(sketch, "E95", {"start": v(82.7, -7.17) * mm, "end": v(153.05, -7.17) * mm});
            skLineSegment(sketch, "E96", {"start": v(153.05, -7.17) * mm, "end": v(153.05, -0.17) * mm});
            skLineSegment(sketch, "E97.bottom", {"start": v(79.6, 10.19) * mm, "end": v(156.15, 10.19) * mm});
            skLineSegment(sketch, "E97.top", {"start": v(79.6, -8.8) * mm, "end": v(156.15, -8.8) * mm});
            skLineSegment(sketch, "E97.left", {"start": v(79.6, 10.19) * mm, "end": v(79.6, -8.8) * mm});
            skLineSegment(sketch, "E97.right", {"start": v(156.15, 10.19) * mm, "end": v(156.15, -8.8) * mm});
            skSolve(sketch);
        }
        {
            var Q0;
            Q0=qSketchRegion(id+"F38",true);
            extrude(context, id + "F39", {"entities" : qUnion([Q0]), "operationType" : NewBodyOperationType.ADD, "depth" : 2 * mm});
        }
        {
            var Q0;
            Q0=makeQuery(id+"F37.opExtrude","CAP_FACE",FACE,{"disambiguationData":[OSD([sQuery(id+"F36.wireOp",EDGE,"E90.bottom"),sQuery(id+"F36.wireOp",EDGE,"E90.top"),sQuery(id+"F36.wireOp",EDGE,"E90.left"),sQuery(id+"F36.wireOp",EDGE,"E90.right")])],"isStart":true});
            var sketch = newSketch(context, id + "F40", { "sketchPlane" : qUnion([Q0])});
            skLineSegment(sketch, "E98.bottom", {"start": v(-157.87, -191.31) * mm, "end": v(-274.87, -191.31) * mm});
            skLineSegment(sketch, "E98.top", {"start": v(-157.87, -148.81) * mm, "end": v(-274.87, -148.81) * mm});
            skLineSegment(sketch, "E98.left", {"start": v(-157.87, -191.31) * mm, "end": v(-157.87, -148.81) * mm});
            skLineSegment(sketch, "E98.right", {"start": v(-274.87, -191.31) * mm, "end": v(-274.87, -148.81) * mm});
            skLineSegment(sketch, "E99.bottom", {"start": v(-273.87, -149.81) * mm, "end": v(-158.87, -149.81) * mm});
            skLineSegment(sketch, "E99.top", {"start": v(-273.87, -190.31) * mm, "end": v(-158.87, -190.31) * mm});
            skLineSegment(sketch, "E99.left", {"start": v(-273.87, -149.81) * mm, "end": v(-273.87, -190.31) * mm});
            skLineSegment(sketch, "E99.right", {"start": v(-158.87, -149.81) * mm, "end": v(-158.87, -190.31) * mm});
            skSolve(sketch);
        }
        {
            var Q0;
            Q0=qSketchRegion(id+"F40",true);
            extrude(context, id + "F41", {"entities" : qUnion([Q0]), "operationType" : NewBodyOperationType.ADD, "depth" : 2 * mm});
        }
        {
            var Q0;
            Q0=makeQuery(id+"F37.opExtrude","CAP_FACE",FACE,{"disambiguationData":[OSD([sQuery(id+"F36.wireOp",EDGE,"E90.bottom"),sQuery(id+"F36.wireOp",EDGE,"E90.top"),sQuery(id+"F36.wireOp",EDGE,"E90.left"),sQuery(id+"F36.wireOp",EDGE,"E90.right")])],"isStart":false});
            extrude(context, id + "F42", {"entities" : qUnion([Q0]), "operationType" : NewBodyOperationType.ADD, "depth" : 1 * mm, "hasDraft" : true, "draftAngle" : 65 * degree, "draftPullDirection" : true});
        }
        {
            var Q0;
            Q0=makeQuery(id+"F42.opExtrude","CAP_FACE",FACE,{"disambiguationData":[OSD([sQuery(id+"F36.wireOp",EDGE,"E90.bottom"),sQuery(id+"F36.wireOp",EDGE,"E90.top"),sQuery(id+"F36.wireOp",EDGE,"E90.left"),sQuery(id+"F36.wireOp",EDGE,"E90.right")])],"isStart":false});
            var sketch = newSketch(context, id + "F43", { "sketchPlane" : qUnion([Q0])});
            skCircle(sketch, "E100", {"center": v(181.37, -173.3) * mm, "radius": 10.5 * mm});
            skCircle(sketch, "E101", {"center": v(214.87, -173.3) * mm, "radius": 10.5 * mm});
            skCircle(sketch, "E102", {"center": v(248.37, -173.3) * mm, "radius": 10.5 * mm});
            skCircle(sketch, "E103", {"center": v(161.37, -152.31) * mm, "radius": 1.1 * mm});
            skCircle(sketch, "E104", {"center": v(271.37, -187.81) * mm, "radius": 1.1 * mm});
            skSolve(sketch);
        }
        {
            var Q0;
            Q0=qSketchRegion(id+"F43",true);
            extrude(context, id + "F44", {"entities" : qUnion([Q0]), "operationType" : NewBodyOperationType.REMOVE, "oppositeDirection" : true, "depth" : 10 * mm, "hasSecondDirection" : true, "secondDirectionOppositeDirection" : false, "secondDirectionDepth" : 10 * mm});
        }
        {
            var Q0;
            Q0=makeQuery(id+"F2.opShell","OFFSET_FACE",FACE,{"disambiguationData":[OSD([sQuery(id+"F0.wireOp",EDGE,"E0.bottom"),sQuery(id+"F0.wireOp",EDGE,"E0.top"),sQuery(id+"F0.wireOp",EDGE,"E0.left"),sQuery(id+"F0.wireOp",EDGE,"E0.right")])]});
            var sketch = newSketch(context, id + "F45", { "sketchPlane" : qUnion([Q0])});
            skLineSegment(sketch, "E105.bottom", {"start": v(-207.56, 81.69) * mm, "end": v(-101.56, 81.69) * mm});
            skLineSegment(sketch, "E105.top", {"start": v(-207.56, -28.31) * mm, "end": v(-101.56, -28.31) * mm});
            skLineSegment(sketch, "E105.left", {"start": v(-207.56, 81.69) * mm, "end": v(-207.56, -28.31) * mm});
            skLineSegment(sketch, "E105.right", {"start": v(-101.56, 81.69) * mm, "end": v(-101.56, -28.31) * mm});
            skSolve(sketch);
        }
        {
            var Q0;
            Q0=qSketchRegion(id+"F45",true);
            extrude(context, id + "F46", {"entities" : qUnion([Q0]), "depth" : 1 * mm});
        }
        {
            var Q0;
            Q0=makeQuery(id+"F44.boolean.opBoolean","INTERSECT",EDGE,{"derivedFrom":[makeQuery(id+"F42.opExtrude","CAP_FACE",FACE,{"disambiguationData":[OSD([sQuery(id+"F36.wireOp",EDGE,"E90.bottom"),sQuery(id+"F36.wireOp",EDGE,"E90.top"),sQuery(id+"F36.wireOp",EDGE,"E90.left"),sQuery(id+"F36.wireOp",EDGE,"E90.right")])],"isStart":false}),makeQuery(id+"F44.opExtrude","SWEPT_FACE",FACE,{"disambiguationData":[OSD([sQuery(id+"F43.wireOp",EDGE,"E102")])]})]});
            var Q1;
            Q1=makeQuery(id+"F44.boolean.opBoolean","INTERSECT",EDGE,{"derivedFrom":[makeQuery(id+"F42.opExtrude","CAP_FACE",FACE,{"disambiguationData":[OSD([sQuery(id+"F36.wireOp",EDGE,"E90.bottom"),sQuery(id+"F36.wireOp",EDGE,"E90.top"),sQuery(id+"F36.wireOp",EDGE,"E90.left"),sQuery(id+"F36.wireOp",EDGE,"E90.right")])],"isStart":false}),makeQuery(id+"F44.opExtrude","SWEPT_FACE",FACE,{"disambiguationData":[OSD([sQuery(id+"F43.wireOp",EDGE,"E101")])]})]});
            var Q2;
            Q2=makeQuery(id+"F44.boolean.opBoolean","INTERSECT",EDGE,{"derivedFrom":[makeQuery(id+"F42.opExtrude","CAP_FACE",FACE,{"disambiguationData":[OSD([sQuery(id+"F36.wireOp",EDGE,"E90.bottom"),sQuery(id+"F36.wireOp",EDGE,"E90.top"),sQuery(id+"F36.wireOp",EDGE,"E90.left"),sQuery(id+"F36.wireOp",EDGE,"E90.right")])],"isStart":false}),makeQuery(id+"F44.opExtrude","SWEPT_FACE",FACE,{"disambiguationData":[OSD([sQuery(id+"F43.wireOp",EDGE,"E100")])]})]});
            chamfer(context, id + "F47", {"entities" : qUnion([Q0, Q1, Q2]), "width" : 1.5 * mm, "tangentPropagation" : true});
        }
        {
            var Q0;
            {var subQ4=makeQuery(id+"F28.opExtrude","SWEPT_FACE",FACE,{"disambiguationData":[OSD([sQuery(id+"F27.wireOp",EDGE,"E76")])]});Q0=makeQuery(id+"F30.boolean.opBoolean","SPLIT",FACE,{"disambiguationData":[TD([subQ4])],"derivedFrom":makeQuery(id+"F28.boolean.opBoolean","SPLIT",FACE,{"disambiguationData":[TD([makeQuery(id+"F28.opExtrude","SWEPT_FACE",FACE,{"disambiguationData":[OSD([sQuery(id+"F27.wireOp",EDGE,"E74")])]})])],"derivedFrom":makeQuery(id+"F24.opExtrude","CAP_FACE",FACE,{"disambiguationData":[OSD([sQuery(id+"F23.wireOp",EDGE,"E64.bottom"),sQuery(id+"F23.wireOp",EDGE,"E64.top"),sQuery(id+"F23.wireOp",EDGE,"E64.left"),sQuery(id+"F23.wireOp",EDGE,"E64.right")])],"isStart":true})})});}
            extrude(context, id + "F48", {"entities" : qUnion([Q0]), "operationType" : NewBodyOperationType.ADD, "depth" : 1 * mm});
        }
        {
            var Q0;
            {var subQ0=sQuery(id+"F23.wireOp",EDGE,"E64.right");var subQ1=sQuery(id+"F23.wireOp",EDGE,"E64.left");var subQ2=sQuery(id+"F23.wireOp",EDGE,"E64.top");var subQ3=sQuery(id+"F23.wireOp",EDGE,"E64.bottom");Q0=makeQuery(id+"F39.boolean.opBoolean","SPLIT",FACE,{"disambiguationData":[TD([makeQuery(id+"F26.boolean.opBoolean","COPY",FACE,{"disambiguationData":[TD([makeQuery(id+"F24.opExtrude","CAP_FACE",FACE,{"disambiguationData":[OSD([subQ3,subQ2,subQ1,subQ0])],"isStart":true})])],"derivedFrom":makeQuery(id+"F26.opExtrude","SWEPT_FACE",FACE,{"disambiguationData":[OSD([sQuery(id+"F25.wireOp",EDGE,"E65")])]})})])],"derivedFrom":makeQuery(id+"F39.opExtrude","CAP_FACE",FACE,{"disambiguationData":[OSD([sQuery(id+"F38.wireOp",EDGE,"E91"),sQuery(id+"F38.wireOp",EDGE,"E92"),sQuery(id+"F38.wireOp",EDGE,"E93"),sQuery(id+"F38.wireOp",EDGE,"E94"),sQuery(id+"F38.wireOp",EDGE,"E95"),sQuery(id+"F38.wireOp",EDGE,"E96"),sQuery(id+"F38.wireOp",EDGE,"E97.bottom"),sQuery(id+"F38.wireOp",EDGE,"E97.top"),sQuery(id+"F38.wireOp",EDGE,"E97.left"),sQuery(id+"F38.wireOp",EDGE,"E97.right")])],"isStart":true})});}
            var Q1;
            {var subQ0=sQuery(id+"F23.wireOp",EDGE,"E64.right");var subQ1=sQuery(id+"F23.wireOp",EDGE,"E64.left");var subQ2=sQuery(id+"F23.wireOp",EDGE,"E64.top");var subQ3=sQuery(id+"F23.wireOp",EDGE,"E64.bottom");Q1=makeQuery(id+"F39.boolean.opBoolean","SPLIT",FACE,{"disambiguationData":[TD([makeQuery(id+"F26.boolean.opBoolean","COPY",FACE,{"disambiguationData":[TD([makeQuery(id+"F24.opExtrude","CAP_FACE",FACE,{"disambiguationData":[OSD([subQ3,subQ2,subQ1,subQ0])],"isStart":true})])],"derivedFrom":makeQuery(id+"F26.opExtrude","SWEPT_FACE",FACE,{"disambiguationData":[OSD([sQuery(id+"F25.wireOp",EDGE,"E67")])]})})])],"derivedFrom":makeQuery(id+"F39.opExtrude","CAP_FACE",FACE,{"disambiguationData":[OSD([sQuery(id+"F38.wireOp",EDGE,"E91"),sQuery(id+"F38.wireOp",EDGE,"E92"),sQuery(id+"F38.wireOp",EDGE,"E93"),sQuery(id+"F38.wireOp",EDGE,"E94"),sQuery(id+"F38.wireOp",EDGE,"E95"),sQuery(id+"F38.wireOp",EDGE,"E96"),sQuery(id+"F38.wireOp",EDGE,"E97.bottom"),sQuery(id+"F38.wireOp",EDGE,"E97.top"),sQuery(id+"F38.wireOp",EDGE,"E97.left"),sQuery(id+"F38.wireOp",EDGE,"E97.right")])],"isStart":true})});}
            extrude(context, id + "F49", {"entities" : qUnion([Q0, Q1]), "operationType" : NewBodyOperationType.REMOVE, "oppositeDirection" : true, "depth" : 2 * mm});
        }
        {
            var Q0;
            Q0=makeQuery(id+"F46.opExtrude","CAP_FACE",FACE,{"disambiguationData":[OSD([sQuery(id+"F45.wireOp",EDGE,"E105.bottom"),sQuery(id+"F45.wireOp",EDGE,"E105.top"),sQuery(id+"F45.wireOp",EDGE,"E105.left"),sQuery(id+"F45.wireOp",EDGE,"E105.right")])],"isStart":true});
            var sketch = newSketch(context, id + "F50", { "sketchPlane" : qUnion([Q0])});
            skLineSegment(sketch, "E106.bottom", {"start": v(125.93, 72.69) * mm, "end": v(183.3, 72.69) * mm});
            skLineSegment(sketch, "E106.top", {"start": v(125.93, 9.69) * mm, "end": v(183.3, 9.69) * mm});
            skLineSegment(sketch, "E106.left", {"start": v(114.62, 61.37) * mm, "end": v(114.62, 21) * mm});
            skLineSegment(sketch, "E106.right", {"start": v(194.62, 61.37) * mm, "end": v(194.62, 21) * mm});
            skLineSegment(sketch, "E107", {"start": v(114.62, 61.37) * mm, "end": v(125.93, 72.69) * mm});
            skLineSegment(sketch, "E108", {"start": v(114.62, 21) * mm, "end": v(125.93, 9.69) * mm});
            skLineSegment(sketch, "E109", {"start": v(183.3, 72.69) * mm, "end": v(194.62, 61.37) * mm});
            skLineSegment(sketch, "E110", {"start": v(183.3, 9.69) * mm, "end": v(194.62, 21) * mm});
            skCircle(sketch, "E111", {"center": v(106.12, 78.19) * mm, "radius": 1.1 * mm});
            skCircle(sketch, "E112", {"center": v(203.12, 78.19) * mm, "radius": 1.1 * mm});
            skCircle(sketch, "E113", {"center": v(203.52, -23.81) * mm, "radius": 1.1 * mm});
            skCircle(sketch, "E114", {"center": v(105.72, -23.81) * mm, "radius": 1.1 * mm});
            skSolve(sketch);
        }
        {
            var Q0;
            Q0=makeQuery(id+"F50.imprint","IMPRINT",FACE,{"disambiguationData":[TD([[makeQuery(id+"F50.imprint","IMPRINT",EDGE,{"derivedFrom":sQuery(id+"F50.wireOp",EDGE,"E106.bottom")}),1.0]])]});
            var sketch = newSketch(context, id + "F51", { "sketchPlane" : qUnion([Q0])});
            skLineSegment(sketch, "E115.bottom", {"start": v(114.52, 79.69) * mm, "end": v(194.72, 79.69) * mm, "construction": true});
            skLineSegment(sketch, "E115.top", {"start": v(114.52, -25.31) * mm, "end": v(194.72, -25.31) * mm, "construction": true});
            skLineSegment(sketch, "E115.left", {"start": v(104.62, 69.79) * mm, "end": v(104.62, -15.41) * mm, "construction": true});
            skLineSegment(sketch, "E115.right", {"start": v(204.62, 69.79) * mm, "end": v(204.62, -15.41) * mm, "construction": true});
            skLineSegment(sketch, "E116", {"start": v(104.62, 69.79) * mm, "end": v(114.52, 79.69) * mm, "construction": true});
            skLineSegment(sketch, "E117", {"start": v(104.62, -15.41) * mm, "end": v(114.52, -25.31) * mm, "construction": true});
            skLineSegment(sketch, "E118", {"start": v(194.72, -25.31) * mm, "end": v(204.62, -15.41) * mm, "construction": true});
            skLineSegment(sketch, "E119", {"start": v(194.72, 79.69) * mm, "end": v(204.62, 69.79) * mm, "construction": true});
            skLineSegment(sketch, "E120", {"start": v(104.87, 69.54) * mm, "end": v(114.68, 79.44) * mm});
            skLineSegment(sketch, "E121", {"start": v(114.68, 79.44) * mm, "end": v(194.62, 79.44) * mm});
            skLineSegment(sketch, "E122", {"start": v(194.62, 79.44) * mm, "end": v(204.37, 69.73) * mm});
            skLineSegment(sketch, "E123", {"start": v(204.37, 69.73) * mm, "end": v(204.37, -15.31) * mm});
            skLineSegment(sketch, "E124", {"start": v(204.37, -15.31) * mm, "end": v(194.62, -25.1) * mm});
            skLineSegment(sketch, "E125", {"start": v(194.62, -25.1) * mm, "end": v(114.66, -25.1) * mm});
            skLineSegment(sketch, "E126", {"start": v(114.66, -25.1) * mm, "end": v(104.87, -15.2) * mm});
            skLineSegment(sketch, "E127", {"start": v(104.87, -15.2) * mm, "end": v(104.87, 69.54) * mm});
            skSolve(sketch);
        }
        {
            var Q0;
            Q0=qSketchRegion(id+"F51",true);
            extrude(context, id + "F52", {"entities" : qUnion([Q0]), "operationType" : NewBodyOperationType.ADD, "depth" : 2 * mm});
        }
        {
            var Q0;
            Q0=qSketchRegion(id+"F50",true);
            extrude(context, id + "F53", {"entities" : qUnion([Q0]), "operationType" : NewBodyOperationType.REMOVE, "depth" : 5 * mm, "hasSecondDirection" : true, "secondDirectionOppositeDirection" : true, "secondDirectionDepth" : 5 * mm});
        }
        {
            var Q0;
            Q0=makeQuery(id+"F52.opExtrude","CAP_FACE",FACE,{"disambiguationData":[OSD([sQuery(id+"F51.wireOp",EDGE,"E120"),sQuery(id+"F51.wireOp",EDGE,"E121"),sQuery(id+"F51.wireOp",EDGE,"E122"),sQuery(id+"F51.wireOp",EDGE,"E123"),sQuery(id+"F51.wireOp",EDGE,"E124"),sQuery(id+"F51.wireOp",EDGE,"E125"),sQuery(id+"F51.wireOp",EDGE,"E126"),sQuery(id+"F51.wireOp",EDGE,"E127")])],"isStart":false});
            var sketch = newSketch(context, id + "F54", { "sketchPlane" : qUnion([Q0])});
            skLineSegment(sketch, "E128", {"start": v(112.62, 62.2) * mm, "end": v(125.1, 74.69) * mm});
            skLineSegment(sketch, "E129", {"start": v(125.1, 74.69) * mm, "end": v(184.14, 74.69) * mm});
            skLineSegment(sketch, "E130", {"start": v(184.14, 74.69) * mm, "end": v(196.62, 62.2) * mm});
            skLineSegment(sketch, "E131", {"start": v(196.62, 62.2) * mm, "end": v(196.62, 20.17) * mm});
            skLineSegment(sketch, "E132", {"start": v(196.62, 20.17) * mm, "end": v(184.14, 7.69) * mm});
            skLineSegment(sketch, "E133", {"start": v(184.14, 7.69) * mm, "end": v(125.1, 7.69) * mm});
            skLineSegment(sketch, "E134", {"start": v(125.1, 7.69) * mm, "end": v(112.62, 20.17) * mm});
            skLineSegment(sketch, "E135", {"start": v(112.62, 20.17) * mm, "end": v(112.62, 62.2) * mm});
            skLineSegment(sketch, "E136", {"start": v(114.62, 61.37) * mm, "end": v(125.93, 72.69) * mm});
            skLineSegment(sketch, "E137", {"start": v(125.93, 72.69) * mm, "end": v(183.3, 72.69) * mm});
            skLineSegment(sketch, "E138", {"start": v(183.3, 72.69) * mm, "end": v(194.62, 61.37) * mm});
            skLineSegment(sketch, "E139", {"start": v(194.62, 61.37) * mm, "end": v(194.62, 21) * mm});
            skLineSegment(sketch, "E140", {"start": v(194.62, 21) * mm, "end": v(183.3, 9.69) * mm});
            skLineSegment(sketch, "E141", {"start": v(183.3, 9.69) * mm, "end": v(125.93, 9.69) * mm});
            skLineSegment(sketch, "E142", {"start": v(125.93, 9.69) * mm, "end": v(114.62, 21) * mm});
            skLineSegment(sketch, "E143", {"start": v(114.62, 21) * mm, "end": v(114.62, 61.37) * mm});
            skSolve(sketch);
        }
        {
            var Q0;
            Q0=makeQuery(id+"F52.opExtrude","CAP_FACE",FACE,{"disambiguationData":[OSD([sQuery(id+"F51.wireOp",EDGE,"E120"),sQuery(id+"F51.wireOp",EDGE,"E121"),sQuery(id+"F51.wireOp",EDGE,"E122"),sQuery(id+"F51.wireOp",EDGE,"E123"),sQuery(id+"F51.wireOp",EDGE,"E124"),sQuery(id+"F51.wireOp",EDGE,"E125"),sQuery(id+"F51.wireOp",EDGE,"E126"),sQuery(id+"F51.wireOp",EDGE,"E127")])],"isStart":false});
            var sketch = newSketch(context, id + "F55", { "sketchPlane" : qUnion([Q0])});
            skLineSegment(sketch, "E144", {"start": v(106.87, 68.72) * mm, "end": v(115.51, 77.44) * mm});
            skLineSegment(sketch, "E145", {"start": v(115.51, 77.44) * mm, "end": v(193.8, 77.44) * mm});
            skLineSegment(sketch, "E146", {"start": v(193.8, 77.44) * mm, "end": v(202.37, 68.9) * mm});
            skLineSegment(sketch, "E147", {"start": v(202.37, 68.9) * mm, "end": v(202.37, -14.49) * mm});
            skLineSegment(sketch, "E148", {"start": v(202.37, -14.49) * mm, "end": v(193.79, -23.1) * mm});
            skLineSegment(sketch, "E149", {"start": v(193.79, -23.1) * mm, "end": v(115.5, -23.1) * mm});
            skLineSegment(sketch, "E150", {"start": v(115.5, -23.1) * mm, "end": v(106.87, -14.37) * mm});
            skLineSegment(sketch, "E151", {"start": v(106.87, -14.37) * mm, "end": v(106.87, 68.72) * mm});
            skLineSegment(sketch, "E152", {"start": v(104.87, 69.54) * mm, "end": v(114.68, 79.44) * mm});
            skLineSegment(sketch, "E153", {"start": v(114.68, 79.44) * mm, "end": v(194.62, 79.44) * mm});
            skLineSegment(sketch, "E154", {"start": v(194.62, 79.44) * mm, "end": v(204.37, 69.73) * mm});
            skLineSegment(sketch, "E155", {"start": v(204.37, 69.73) * mm, "end": v(204.37, -15.31) * mm});
            skLineSegment(sketch, "E156", {"start": v(204.37, -15.31) * mm, "end": v(194.62, -25.1) * mm});
            skLineSegment(sketch, "E157", {"start": v(194.62, -25.1) * mm, "end": v(114.66, -25.1) * mm});
            skLineSegment(sketch, "E158", {"start": v(114.66, -25.1) * mm, "end": v(104.87, -15.2) * mm});
            skLineSegment(sketch, "E159", {"start": v(104.87, -15.2) * mm, "end": v(104.87, 69.54) * mm});
            skSolve(sketch);
        }
        {
            var Q0;
            Q0=qSketchRegion(id+"F54",true);
            extrude(context, id + "F56", {"entities" : qUnion([Q0]), "operationType" : NewBodyOperationType.ADD, "oppositeDirection" : true, "depth" : 5 * mm});
        }
        {
            var Q0;
            Q0=qSketchRegion(id+"F55",true);
            extrude(context, id + "F57", {"entities" : qUnion([Q0]), "operationType" : NewBodyOperationType.ADD, "depth" : 1 * mm});
        }
        {
            var Q0;
            Q0=makeQuery(id+"F52.opExtrude","CAP_FACE",FACE,{"disambiguationData":[OSD([sQuery(id+"F51.wireOp",EDGE,"E120"),sQuery(id+"F51.wireOp",EDGE,"E121"),sQuery(id+"F51.wireOp",EDGE,"E122"),sQuery(id+"F51.wireOp",EDGE,"E123"),sQuery(id+"F51.wireOp",EDGE,"E124"),sQuery(id+"F51.wireOp",EDGE,"E125"),sQuery(id+"F51.wireOp",EDGE,"E126"),sQuery(id+"F51.wireOp",EDGE,"E127")])],"isStart":false});
            var sketch = newSketch(context, id + "F58", { "sketchPlane" : qUnion([Q0])});
            skLineSegment(sketch, "E160.left", {"start": v(137.62, 6.69) * mm, "end": v(137.62, 1.69) * mm});
            skLineSegment(sketch, "E160.right", {"start": v(171.62, 6.69) * mm, "end": v(171.62, 1.69) * mm});
            skArc(sketch, "E161", {"start": v(137.62, 6.69) * mm, "mid": v(154.62, 4) * mm, "end": v(171.62, 6.69) * mm});
            skArc(sketch, "E162", {"start": v(137.62, 1.69) * mm, "mid": v(154.62, -0.77) * mm, "end": v(171.62, 1.69) * mm});
            skSolve(sketch);
        }
        {
            var Q0;
            Q0=qSketchRegion(id+"F58",true);
            extrude(context, id + "F59", {"entities" : qUnion([Q0]), "operationType" : NewBodyOperationType.REMOVE, "oppositeDirection" : true, "depth" : 5 * mm});
        }
        {
            var Q0;
            Q0=makeQuery(id+"F52.opExtrude","CAP_FACE",FACE,{"disambiguationData":[OSD([sQuery(id+"F51.wireOp",EDGE,"E120"),sQuery(id+"F51.wireOp",EDGE,"E121"),sQuery(id+"F51.wireOp",EDGE,"E122"),sQuery(id+"F51.wireOp",EDGE,"E123"),sQuery(id+"F51.wireOp",EDGE,"E124"),sQuery(id+"F51.wireOp",EDGE,"E125"),sQuery(id+"F51.wireOp",EDGE,"E126"),sQuery(id+"F51.wireOp",EDGE,"E127")])],"isStart":false});
            var sketch = newSketch(context, id + "F60", { "sketchPlane" : qUnion([Q0])});
            skLineSegment(sketch, "E163", {"start": v(171.68, 6.7) * mm, "end": v(171.68, 1.7) * mm});
            skFitSpline(sketch, "E164.MirrorCS", {"points": [v(171.68, 6.7) * mm, v(176.37, 7.79) * mm, v(179.09, 5.4) * mm, v(178.01, 2.91) * mm, v(171.68, 1.7) * mm], "startDerivative": vector(18.24, 8) * mm, "endDerivative": vector(-24.25, -1.37) * mm});
            skLineSegment(sketch, "E165", {"start": v(137.58, 6.68) * mm, "end": v(137.58, 1.68) * mm});
            skFitSpline(sketch, "E166.MirrorCS", {"points": [v(137.58, 6.68) * mm, v(132.9, 7.78) * mm, v(130.17, 5.39) * mm, v(131.25, 2.9) * mm, v(137.58, 1.68) * mm], "startDerivative": vector(-18.24, 8) * mm, "endDerivative": vector(24.25, -1.37) * mm});
            skSolve(sketch);
        }
        {
            var Q0;
            Q0=makeQuery(id+"F60.imprint","IMPRINT",FACE,{"disambiguationData":[TD([[makeQuery(id+"F60.imprint","IMPRINT",EDGE,{"derivedFrom":sQuery(id+"F60.wireOp",EDGE,"E165")}),-1.0]])]});
            var Q1;
            Q1=makeQuery(id+"F60.imprint","IMPRINT",FACE,{"disambiguationData":[TD([[makeQuery(id+"F60.imprint","IMPRINT",EDGE,{"derivedFrom":sQuery(id+"F60.wireOp",EDGE,"E163")}),1.0]])]});
            var Q2;
            Q2=sQuery(id+"F60.wireOp",EDGE,"daf1eef1-cd77-4b66-a7e7-b0265bb4bf25");
            var Q3;
            Q3=sQuery(id+"F60.wireOp",EDGE,"84O3oZmx-gldQ-fziM-4V3f-qkykIBgHlrQC");
            extrude(context, id + "F61", {"entities" : qUnion([Q0, Q1]), "operationType" : NewBodyOperationType.ADD, "surfaceEntities" : qUnion([Q2, Q3]), "depth" : 2 * mm});
        }
        {
            var Q0;
            Q0=makeQuery(id+"F61.opExtrude","CAP_EDGE",EDGE,{"disambiguationData":[OSD([sQuery(id+"F60.wireOp",EDGE,"E166.MirrorCS")])],"isStart":false});
            var Q1;
            Q1=makeQuery(id+"F61.opExtrude","CAP_EDGE",EDGE,{"disambiguationData":[OSD([sQuery(id+"F60.wireOp",EDGE,"E164.MirrorCS")])],"isStart":false});
            fillet(context, id + "F62", {"entities" : qUnion([Q0, Q1]), "radius" : 2 * mm, "tangentPropagation" : true, "allowEdgeOverflow" : false});
        }
        {
            var Q0;
            Q0=makeQuery(id+"F61.opExtrude","CAP_EDGE",EDGE,{"disambiguationData":[OSD([sQuery(id+"F60.wireOp",EDGE,"E165")])],"isStart":false});
            var Q1;
            Q1=makeQuery(id+"F61.opExtrude","CAP_EDGE",EDGE,{"disambiguationData":[OSD([sQuery(id+"F60.wireOp",EDGE,"E163")])],"isStart":false});
            fillet(context, id + "F63", {"entities" : qUnion([Q0, Q1]), "radius" : 1 * mm, "tangentPropagation" : true, "allowEdgeOverflow" : false});
        }
        {
            var Q0;
            Q0=makeQuery(id+"F57.opExtrude","CAP_FACE",FACE,{"disambiguationData":[OSD([sQuery(id+"F55.wireOp",EDGE,"E144"),sQuery(id+"F55.wireOp",EDGE,"E145"),sQuery(id+"F55.wireOp",EDGE,"E146"),sQuery(id+"F55.wireOp",EDGE,"E147"),sQuery(id+"F55.wireOp",EDGE,"E148"),sQuery(id+"F55.wireOp",EDGE,"E149"),sQuery(id+"F55.wireOp",EDGE,"E150"),sQuery(id+"F55.wireOp",EDGE,"E151"),sQuery(id+"F55.wireOp",EDGE,"E152"),sQuery(id+"F55.wireOp",EDGE,"E153"),sQuery(id+"F55.wireOp",EDGE,"E154"),sQuery(id+"F55.wireOp",EDGE,"E155"),sQuery(id+"F55.wireOp",EDGE,"E156"),sQuery(id+"F55.wireOp",EDGE,"E157"),sQuery(id+"F55.wireOp",EDGE,"E158"),sQuery(id+"F55.wireOp",EDGE,"E159")])],"isStart":false});
            var sketch = newSketch(context, id + "F64", { "sketchPlane" : qUnion([Q0])});
            skLineSegment(sketch, "E167.bottom", {"start": v(116.13, -19.46) * mm, "end": v(193.2, -19.46) * mm});
            skLineSegment(sketch, "E167.top", {"start": v(116.13, -28.09) * mm, "end": v(193.2, -28.09) * mm});
            skLineSegment(sketch, "E167.left", {"start": v(116.13, -19.46) * mm, "end": v(116.13, -28.09) * mm});
            skLineSegment(sketch, "E167.right", {"start": v(193.2, -19.46) * mm, "end": v(193.2, -28.09) * mm});
            skSolve(sketch);
        }
        {
            var Q0;
            Q0=qSketchRegion(id+"F64",true);
            extrude(context, id + "F65", {"entities" : qUnion([Q0]), "operationType" : NewBodyOperationType.REMOVE, "oppositeDirection" : true, "depth" : 1 * mm});
        }
        {
            var Q0;
            Q0=makeQuery(id+"F52.opExtrude","CAP_FACE",FACE,{"disambiguationData":[OSD([sQuery(id+"F51.wireOp",EDGE,"E120"),sQuery(id+"F51.wireOp",EDGE,"E121"),sQuery(id+"F51.wireOp",EDGE,"E122"),sQuery(id+"F51.wireOp",EDGE,"E123"),sQuery(id+"F51.wireOp",EDGE,"E124"),sQuery(id+"F51.wireOp",EDGE,"E125"),sQuery(id+"F51.wireOp",EDGE,"E126"),sQuery(id+"F51.wireOp",EDGE,"E127")])],"isStart":false});
            var sketch = newSketch(context, id + "F66", { "sketchPlane" : qUnion([Q0])});
            skCircle(sketch, "E168", {"center": v(191.08, -21.73) * mm, "radius": 1.5 * mm});
            skCircle(sketch, "E169", {"center": v(184.33, -21.73) * mm, "radius": 3 * mm});
            skCircle(sketch, "E170", {"center": v(161.08, -21.73) * mm, "radius": 1.5 * mm});
            skLineSegment(sketch, "E171.bottom", {"start": v(158.5, -16.35) * mm, "end": v(193.45, -16.35) * mm, "construction": true});
            skLineSegment(sketch, "E171.top", {"start": v(158.5, -26.05) * mm, "end": v(193.45, -26.05) * mm, "construction": true});
            skLineSegment(sketch, "E171.left", {"start": v(158.5, -16.35) * mm, "end": v(158.5, -26.05) * mm, "construction": true});
            skLineSegment(sketch, "E171.right", {"start": v(193.45, -16.35) * mm, "end": v(193.45, -26.05) * mm, "construction": true});
            skSolve(sketch);
        }
        {
            var Q0;
            Q0=qSketchRegion(id+"F66",true);
            extrude(context, id + "F67", {"entities" : qUnion([Q0]), "operationType" : NewBodyOperationType.REMOVE, "oppositeDirection" : true, "depth" : 5 * mm});
        }
        {
            var Q0;
            Q0=makeQuery(id+"F52.opExtrude","CAP_FACE",FACE,{"disambiguationData":[OSD([sQuery(id+"F51.wireOp",EDGE,"E120"),sQuery(id+"F51.wireOp",EDGE,"E121"),sQuery(id+"F51.wireOp",EDGE,"E122"),sQuery(id+"F51.wireOp",EDGE,"E123"),sQuery(id+"F51.wireOp",EDGE,"E124"),sQuery(id+"F51.wireOp",EDGE,"E125"),sQuery(id+"F51.wireOp",EDGE,"E126"),sQuery(id+"F51.wireOp",EDGE,"E127")])],"isStart":false});
            var sketch = newSketch(context, id + "F68", { "sketchPlane" : qUnion([Q0])});
            skLineSegment(sketch, "E172.bottom", {"start": v(144.84, -2.25) * mm, "end": v(162.84, -2.25) * mm});
            skLineSegment(sketch, "E172.top", {"start": v(144.84, -19.25) * mm, "end": v(162.84, -19.25) * mm});
            skLineSegment(sketch, "E172.left", {"start": v(144.84, -2.25) * mm, "end": v(144.84, -19.25) * mm});
            skLineSegment(sketch, "E172.right", {"start": v(162.84, -2.25) * mm, "end": v(162.84, -19.25) * mm});
            skCircle(sketch, "E173", {"center": v(142.84, -6.25) * mm, "radius": 1 * mm});
            skCircle(sketch, "E174", {"center": v(142.84, -15.25) * mm, "radius": 1 * mm});
            skCircle(sketch, "E175", {"center": v(164.84, -6.25) * mm, "radius": 1 * mm});
            skCircle(sketch, "E176", {"center": v(164.84, -15.25) * mm, "radius": 1 * mm});
            skSolve(sketch);
        }
        {
            var Q0;
            Q0=qSketchRegion(id+"F68",true);
            extrude(context, id + "F69", {"entities" : qUnion([Q0]), "operationType" : NewBodyOperationType.REMOVE, "oppositeDirection" : true, "depth" : 5 * mm});
        }
        {
            var Q0;
            Q0=makeQuery(id+"F53.boolean.opBoolean","INTERSECT",EDGE,{"derivedFrom":[makeQuery(id+"F52.opExtrude","CAP_FACE",FACE,{"disambiguationData":[OSD([sQuery(id+"F51.wireOp",EDGE,"E120"),sQuery(id+"F51.wireOp",EDGE,"E121"),sQuery(id+"F51.wireOp",EDGE,"E122"),sQuery(id+"F51.wireOp",EDGE,"E123"),sQuery(id+"F51.wireOp",EDGE,"E124"),sQuery(id+"F51.wireOp",EDGE,"E125"),sQuery(id+"F51.wireOp",EDGE,"E126"),sQuery(id+"F51.wireOp",EDGE,"E127")])],"isStart":false}),makeQuery(id+"F53.opExtrude","SWEPT_FACE",FACE,{"disambiguationData":[OSD([sQuery(id+"F50.wireOp",EDGE,"E106.bottom")])]})]});
            var Q1;
            Q1=makeQuery(id+"F53.boolean.opBoolean","INTERSECT",EDGE,{"derivedFrom":[makeQuery(id+"F52.opExtrude","CAP_FACE",FACE,{"disambiguationData":[OSD([sQuery(id+"F51.wireOp",EDGE,"E120"),sQuery(id+"F51.wireOp",EDGE,"E121"),sQuery(id+"F51.wireOp",EDGE,"E122"),sQuery(id+"F51.wireOp",EDGE,"E123"),sQuery(id+"F51.wireOp",EDGE,"E124"),sQuery(id+"F51.wireOp",EDGE,"E125"),sQuery(id+"F51.wireOp",EDGE,"E126"),sQuery(id+"F51.wireOp",EDGE,"E127")])],"isStart":false}),makeQuery(id+"F53.opExtrude","SWEPT_FACE",FACE,{"disambiguationData":[OSD([sQuery(id+"F50.wireOp",EDGE,"E107")])]})]});
            var Q2;
            Q2=makeQuery(id+"F53.boolean.opBoolean","INTERSECT",EDGE,{"derivedFrom":[makeQuery(id+"F52.opExtrude","CAP_FACE",FACE,{"disambiguationData":[OSD([sQuery(id+"F51.wireOp",EDGE,"E120"),sQuery(id+"F51.wireOp",EDGE,"E121"),sQuery(id+"F51.wireOp",EDGE,"E122"),sQuery(id+"F51.wireOp",EDGE,"E123"),sQuery(id+"F51.wireOp",EDGE,"E124"),sQuery(id+"F51.wireOp",EDGE,"E125"),sQuery(id+"F51.wireOp",EDGE,"E126"),sQuery(id+"F51.wireOp",EDGE,"E127")])],"isStart":false}),makeQuery(id+"F53.opExtrude","SWEPT_FACE",FACE,{"disambiguationData":[OSD([sQuery(id+"F50.wireOp",EDGE,"E106.left")])]})]});
            var Q3;
            Q3=makeQuery(id+"F53.boolean.opBoolean","INTERSECT",EDGE,{"derivedFrom":[makeQuery(id+"F52.opExtrude","CAP_FACE",FACE,{"disambiguationData":[OSD([sQuery(id+"F51.wireOp",EDGE,"E120"),sQuery(id+"F51.wireOp",EDGE,"E121"),sQuery(id+"F51.wireOp",EDGE,"E122"),sQuery(id+"F51.wireOp",EDGE,"E123"),sQuery(id+"F51.wireOp",EDGE,"E124"),sQuery(id+"F51.wireOp",EDGE,"E125"),sQuery(id+"F51.wireOp",EDGE,"E126"),sQuery(id+"F51.wireOp",EDGE,"E127")])],"isStart":false}),makeQuery(id+"F53.opExtrude","SWEPT_FACE",FACE,{"disambiguationData":[OSD([sQuery(id+"F50.wireOp",EDGE,"E108")])]})]});
            var Q4;
            Q4=makeQuery(id+"F53.boolean.opBoolean","INTERSECT",EDGE,{"derivedFrom":[makeQuery(id+"F52.opExtrude","CAP_FACE",FACE,{"disambiguationData":[OSD([sQuery(id+"F51.wireOp",EDGE,"E120"),sQuery(id+"F51.wireOp",EDGE,"E121"),sQuery(id+"F51.wireOp",EDGE,"E122"),sQuery(id+"F51.wireOp",EDGE,"E123"),sQuery(id+"F51.wireOp",EDGE,"E124"),sQuery(id+"F51.wireOp",EDGE,"E125"),sQuery(id+"F51.wireOp",EDGE,"E126"),sQuery(id+"F51.wireOp",EDGE,"E127")])],"isStart":false}),makeQuery(id+"F53.opExtrude","SWEPT_FACE",FACE,{"disambiguationData":[OSD([sQuery(id+"F50.wireOp",EDGE,"E106.top")])]})]});
            var Q5;
            Q5=makeQuery(id+"F53.boolean.opBoolean","INTERSECT",EDGE,{"derivedFrom":[makeQuery(id+"F52.opExtrude","CAP_FACE",FACE,{"disambiguationData":[OSD([sQuery(id+"F51.wireOp",EDGE,"E120"),sQuery(id+"F51.wireOp",EDGE,"E121"),sQuery(id+"F51.wireOp",EDGE,"E122"),sQuery(id+"F51.wireOp",EDGE,"E123"),sQuery(id+"F51.wireOp",EDGE,"E124"),sQuery(id+"F51.wireOp",EDGE,"E125"),sQuery(id+"F51.wireOp",EDGE,"E126"),sQuery(id+"F51.wireOp",EDGE,"E127")])],"isStart":false}),makeQuery(id+"F53.opExtrude","SWEPT_FACE",FACE,{"disambiguationData":[OSD([sQuery(id+"F50.wireOp",EDGE,"E110")])]})]});
            var Q6;
            Q6=makeQuery(id+"F53.boolean.opBoolean","INTERSECT",EDGE,{"derivedFrom":[makeQuery(id+"F52.opExtrude","CAP_FACE",FACE,{"disambiguationData":[OSD([sQuery(id+"F51.wireOp",EDGE,"E120"),sQuery(id+"F51.wireOp",EDGE,"E121"),sQuery(id+"F51.wireOp",EDGE,"E122"),sQuery(id+"F51.wireOp",EDGE,"E123"),sQuery(id+"F51.wireOp",EDGE,"E124"),sQuery(id+"F51.wireOp",EDGE,"E125"),sQuery(id+"F51.wireOp",EDGE,"E126"),sQuery(id+"F51.wireOp",EDGE,"E127")])],"isStart":false}),makeQuery(id+"F53.opExtrude","SWEPT_FACE",FACE,{"disambiguationData":[OSD([sQuery(id+"F50.wireOp",EDGE,"E106.right")])]})]});
            var Q7;
            Q7=makeQuery(id+"F53.boolean.opBoolean","INTERSECT",EDGE,{"derivedFrom":[makeQuery(id+"F52.opExtrude","CAP_FACE",FACE,{"disambiguationData":[OSD([sQuery(id+"F51.wireOp",EDGE,"E120"),sQuery(id+"F51.wireOp",EDGE,"E121"),sQuery(id+"F51.wireOp",EDGE,"E122"),sQuery(id+"F51.wireOp",EDGE,"E123"),sQuery(id+"F51.wireOp",EDGE,"E124"),sQuery(id+"F51.wireOp",EDGE,"E125"),sQuery(id+"F51.wireOp",EDGE,"E126"),sQuery(id+"F51.wireOp",EDGE,"E127")])],"isStart":false}),makeQuery(id+"F53.opExtrude","SWEPT_FACE",FACE,{"disambiguationData":[OSD([sQuery(id+"F50.wireOp",EDGE,"E109")])]})]});
            chamfer(context, id + "F70", {"entities" : qUnion([Q0, Q1, Q2, Q3, Q4, Q5, Q6, Q7]), "width" : 1 * mm, "tangentPropagation" : true});
        }
        {
            var Q0;
            Q0=makeQuery(id+"F1.opExtrude","SWEPT_FACE",FACE,{"disambiguationData":[OSD([sQuery(id+"F0.wireOp",EDGE,"E0.bottom")])]});
            var sketch = newSketch(context, id + "F71", { "sketchPlane" : qUnion([Q0])});
            skCircle(sketch, "E177", {"center": v(-203.83, -25.04) * mm, "radius": 1.1 * mm});
            skCircle(sketch, "E178", {"center": v(-147.03, -25.04) * mm, "radius": 1.1 * mm});
            skCircle(sketch, "E179", {"center": v(178.36, -25.04) * mm, "radius": 1.1 * mm});
            skCircle(sketch, "E180", {"center": v(121.56, -25.04) * mm, "radius": 1.1 * mm});
            skSolve(sketch);
        }
        {
            var Q0;
            Q0=qSketchRegion(id+"F71",true);
            extrude(context, id + "F72", {"entities" : qUnion([Q0]), "operationType" : NewBodyOperationType.REMOVE, "depth" : 25 * mm, "hasSecondDirection" : true, "secondDirectionOppositeDirection" : true, "secondDirectionDepth" : 150 * mm});
        }
        {
            var Q0;
            Q0=makeQuery(id+"F20.opExtrude","CAP_FACE",FACE,{"disambiguationData":[OSD([sQuery(id+"F19.wireOp",EDGE,"E59.bottom"),sQuery(id+"F19.wireOp",EDGE,"E59.top"),sQuery(id+"F19.wireOp",EDGE,"E59.left"),sQuery(id+"F19.wireOp",EDGE,"E59.right"),sQuery(id+"F19.wireOp",EDGE,"E60.bottom"),sQuery(id+"F19.wireOp",EDGE,"E60.top"),sQuery(id+"F19.wireOp",EDGE,"E60.left"),sQuery(id+"F19.wireOp",EDGE,"E60.right")])],"isStart":false});
            var sketch = newSketch(context, id + "F73", { "sketchPlane" : qUnion([Q0])});
            skLineSegment(sketch, "E181.bottom", {"start": v(166.37, -151.81) * mm, "end": v(266.37, -151.81) * mm});
            skLineSegment(sketch, "E181.top", {"start": v(166.37, -188.31) * mm, "end": v(266.37, -188.31) * mm});
            skLineSegment(sketch, "E181.left", {"start": v(166.37, -151.81) * mm, "end": v(166.37, -188.31) * mm});
            skLineSegment(sketch, "E181.right", {"start": v(266.37, -151.81) * mm, "end": v(266.37, -188.31) * mm});
            skLineSegment(sketch, "E182.bottom", {"start": v(168.37, -153.81) * mm, "end": v(197.62, -153.81) * mm});
            skLineSegment(sketch, "E182.top", {"start": v(168.37, -186.31) * mm, "end": v(197.62, -186.31) * mm});
            skLineSegment(sketch, "E182.left", {"start": v(168.37, -153.81) * mm, "end": v(168.37, -186.31) * mm});
            skLineSegment(sketch, "E182.right", {"start": v(197.62, -153.81) * mm, "end": v(197.62, -186.31) * mm});
            skLineSegment(sketch, "E183.bottom", {"start": v(201.37, -153.81) * mm, "end": v(230.62, -153.81) * mm});
            skLineSegment(sketch, "E183.top", {"start": v(201.37, -186.31) * mm, "end": v(230.62, -186.31) * mm});
            skLineSegment(sketch, "E183.left", {"start": v(201.37, -153.81) * mm, "end": v(201.37, -186.31) * mm});
            skLineSegment(sketch, "E183.right", {"start": v(230.62, -153.81) * mm, "end": v(230.62, -186.31) * mm});
            skLineSegment(sketch, "E184.bottom", {"start": v(234.87, -153.81) * mm, "end": v(264.12, -153.81) * mm});
            skLineSegment(sketch, "E184.top", {"start": v(234.87, -186.31) * mm, "end": v(264.12, -186.31) * mm});
            skLineSegment(sketch, "E184.left", {"start": v(234.87, -153.81) * mm, "end": v(234.87, -186.31) * mm});
            skLineSegment(sketch, "E184.right", {"start": v(264.12, -153.81) * mm, "end": v(264.12, -186.31) * mm});
            skSolve(sketch);
        }
        {
            var Q0;
            Q0=qSketchRegion(id+"F73",true);
            extrude(context, id + "F74", {"entities" : qUnion([Q0]), "depth" : 1 * mm});
        }
    });
